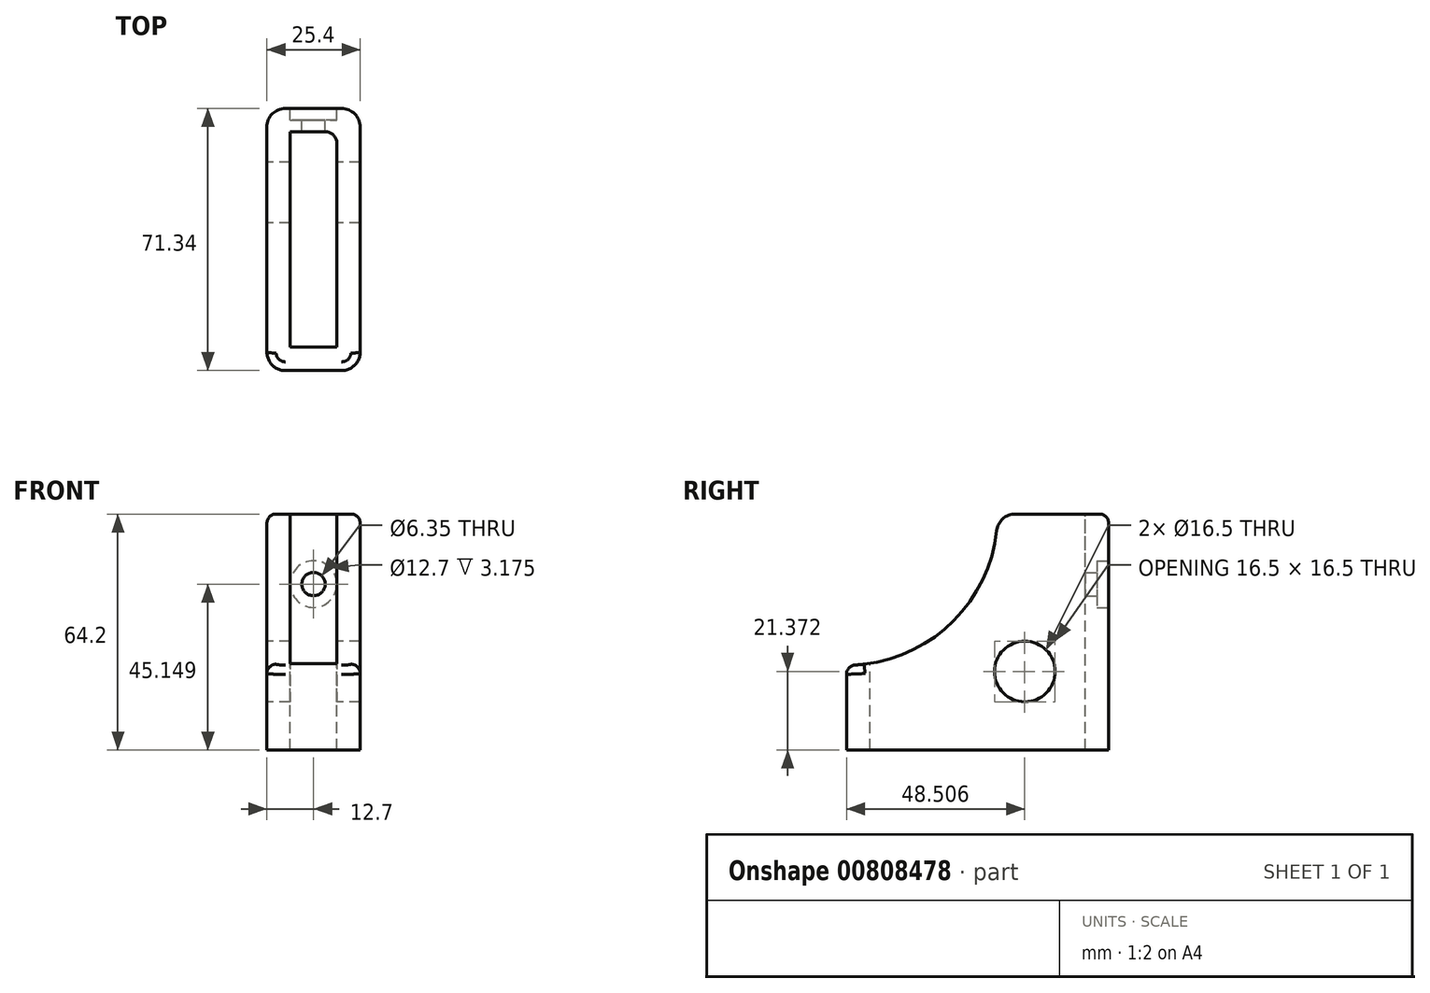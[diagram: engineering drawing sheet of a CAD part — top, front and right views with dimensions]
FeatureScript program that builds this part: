
annotation { "Feature Type Name" : "Feature", "Feature Type Description" : "" }
export const myFeature = defineFeature(function(context is Context, id is Id, definition is map)
    precondition{}
    {
        {
            var Q0;
            Q0=qCreatedBy(makeId("Right.planeOp"),FACE);
            var sketch = newSketch(context, id + "F0", { "sketchPlane" : qUnion([Q0])});
            skLineSegment(sketch, "E0", {"start": v(-41.12, 55.88) * mm, "end": v(-41.12, -8.32) * mm});
            skLineSegment(sketch, "E1", {"start": v(30.22, -8.32) * mm, "end": v(30.22, 55.88) * mm});
            skLineSegment(sketch, "E2", {"start": v(-41.12, 55.88) * mm, "end": v(30.22, 55.88) * mm});
            skLineSegment(sketch, "E3", {"start": v(-41.12, -8.32) * mm, "end": v(30.22, -8.32) * mm});
            skCircle(sketch, "E4", {"center": v(7.39, 13.05) * mm, "radius": 8.25 * mm});
            skSolve(sketch);
        }
        {
            var Q0;
            Q0 = qSketchRegion(id + "F0", true);
            extrude(context, id + "F1", {"entities" : qUnion([Q0]), "depth" : 25.4 * mm, "offsetDistance" : 25.4 * mm});
        }
        {
            var Q0;
            Q0=makeQuery(id+"F1.opExtrude","CAP_FACE",FACE,{"disambiguationData":[OSD([sQuery(id+"F0.wireOp",EDGE,"E0"),sQuery(id+"F0.wireOp",EDGE,"E1"),sQuery(id+"F0.wireOp",EDGE,"E2"),sQuery(id+"F0.wireOp",EDGE,"E3"),sQuery(id+"F0.wireOp",EDGE,"E4")])],"isStart":false});
            var sketch = newSketch(context, id + "F2", { "sketchPlane" : qUnion([Q0])});
            skCircle(sketch, "E5", {"center": v(-41.12, 55.88) * mm, "radius": 41.13 * mm});
            skSolve(sketch);
        }
        {
            var Q0;
            Q0 = qSketchRegion(id + "F2", true);
            extrude(context, id + "F3", {"entities" : qUnion([Q0]), "operationType" : NewBodyOperationType.REMOVE, "endBound" : BoundingType.THROUGH_ALL, "oppositeDirection" : true, "depth" : 25.4 * mm, "offsetDistance" : 25.4 * mm});
        }
        {
            var Q0;
            Q0=makeQuery(id+"F1.opExtrude","SWEPT_FACE",FACE,{"disambiguationData":[OSD([sQuery(id+"F0.wireOp",EDGE,"E2")])]});
            var sketch = newSketch(context, id + "F4", { "sketchPlane" : qUnion([Q0])});
            skLineSegment(sketch, "E6.bottom", {"start": v(6.35, 23.87) * mm, "end": v(19.05, 23.87) * mm});
            skLineSegment(sketch, "E6.top", {"start": v(6.35, -34.77) * mm, "end": v(19.05, -34.77) * mm});
            skLineSegment(sketch, "E6.left", {"start": v(6.35, 23.87) * mm, "end": v(6.35, -34.77) * mm});
            skLineSegment(sketch, "E6.right", {"start": v(19.05, 23.87) * mm, "end": v(19.05, -34.77) * mm});
            skSolve(sketch);
        }
        {
            var Q0;
            {var subQ0=sQuery(id+"F4.wireOp",EDGE,"E6.top");Q0=makeQuery(id+"F4.imprint","IMPRINT",FACE,{"disambiguationData":[TD([[makeQuery(id+"F4.imprint","IMPRINT",EDGE,{"derivedFrom":subQ0}),1.0]])]});}
            var Q1;
            {var subQ0=sQuery(id+"F4.wireOp",EDGE,"E6.bottom");Q1=makeQuery(id+"F4.imprint","IMPRINT",FACE,{"disambiguationData":[TD([[makeQuery(id+"F4.imprint","IMPRINT",EDGE,{"derivedFrom":subQ0}),-1.0]])]});}
            extrude(context, id + "F5", {"entities" : qUnion([Q0, Q1]), "operationType" : NewBodyOperationType.REMOVE, "endBound" : BoundingType.THROUGH_ALL, "oppositeDirection" : true, "depth" : 25.4 * mm, "offsetDistance" : 25.4 * mm});
        }
        {
            var Q0;
            {var subQ0=sQuery(id+"F0.wireOp",EDGE,"E2");var subQ1=makeQuery(id+"F1.opExtrude","SWEPT_FACE",FACE,{"disambiguationData":[OSD([subQ0])]});var subQ2=makeQuery(id+"F3.opExtrude","SWEPT_FACE",FACE,{"disambiguationData":[OSD([sQuery(id+"F2.wireOp",EDGE,"E5")])]});Q0=makeQuery(id+"F5.boolean.opBoolean","SPLIT",EDGE,{"disambiguationData":[TD([makeQuery(id+"F5.opExtrude","SWEPT_FACE",FACE,{"disambiguationData":[OSD([sQuery(id+"F4.wireOp",EDGE,"E6.left")])]})])],"derivedFrom":makeQuery(id+"F3.boolean.opBoolean","INTERSECT",EDGE,{"derivedFrom":[subQ1,subQ2]})});}
            var Q1;
            {var subQ0=sQuery(id+"F0.wireOp",EDGE,"E2");var subQ1=makeQuery(id+"F1.opExtrude","SWEPT_FACE",FACE,{"disambiguationData":[OSD([subQ0])]});var subQ2=makeQuery(id+"F3.opExtrude","SWEPT_FACE",FACE,{"disambiguationData":[OSD([sQuery(id+"F2.wireOp",EDGE,"E5")])]});Q1=makeQuery(id+"F5.boolean.opBoolean","SPLIT",EDGE,{"disambiguationData":[TD([makeQuery(id+"F5.opExtrude","SWEPT_FACE",FACE,{"disambiguationData":[OSD([sQuery(id+"F4.wireOp",EDGE,"E6.right")])]})])],"derivedFrom":makeQuery(id+"F3.boolean.opBoolean","INTERSECT",EDGE,{"derivedFrom":[subQ1,subQ2]})});}
            fillet(context, id + "F6", {"entities" : qUnion([Q0, Q1]), "radius" : 5.08 * mm, "tangentPropagation" : true, "allowEdgeOverflow" : false});
        }
        {
            var Q0;
            Q0=makeQuery(id+"F1.opExtrude","CAP_EDGE",EDGE,{"disambiguationData":[OSD([sQuery(id+"F0.wireOp",EDGE,"E1")])],"isStart":false});
            var Q1;
            Q1=makeQuery(id+"F1.opExtrude","CAP_EDGE",EDGE,{"disambiguationData":[OSD([sQuery(id+"F0.wireOp",EDGE,"E0")])],"isStart":false});
            var Q2;
            Q2=makeQuery(id+"F1.opExtrude","CAP_EDGE",EDGE,{"disambiguationData":[OSD([sQuery(id+"F0.wireOp",EDGE,"E0")])],"isStart":true});
            var Q3;
            Q3=makeQuery(id+"F1.opExtrude","CAP_EDGE",EDGE,{"disambiguationData":[OSD([sQuery(id+"F0.wireOp",EDGE,"E1")])],"isStart":true});
            fillet(context, id + "F7", {"entities" : qUnion([Q0, Q1, Q2, Q3]), "radius" : 5.08 * mm, "tangentPropagation" : true, "allowEdgeOverflow" : false});
        }
        {
            var Q0;
            Q0=makeQuery(id+"F3.boolean.opBoolean","COPY",EDGE,{"derivedFrom":makeQuery(id+"F3.opExtrude","CAP_EDGE",EDGE,{"disambiguationData":[OSD([sQuery(id+"F2.wireOp",EDGE,"E5")])],"isStart":true})});
            var Q1;
            {var subQ0=sQuery(id+"F0.wireOp",EDGE,"E2");var subQ1=makeQuery(id+"F1.opExtrude","CAP_FACE",FACE,{"disambiguationData":[OSD([sQuery(id+"F0.wireOp",EDGE,"E0"),sQuery(id+"F0.wireOp",EDGE,"E1"),subQ0,sQuery(id+"F0.wireOp",EDGE,"E3"),sQuery(id+"F0.wireOp",EDGE,"E4")])],"isStart":false});var subQ2=makeQuery(id+"F1.opExtrude","SWEPT_FACE",FACE,{"disambiguationData":[OSD([subQ0])]});var subQ3=makeQuery(id+"F3.opExtrude","SWEPT_FACE",FACE,{"disambiguationData":[OSD([sQuery(id+"F2.wireOp",EDGE,"E5")])]});Q1=makeQuery(id+"F6.opFillet","BLEND_EDGE",EDGE,{"blendedFrom":[makeQuery(id+"F5.boolean.opBoolean","SPLIT",EDGE,{"disambiguationData":[TD([makeQuery(id+"F5.opExtrude","SWEPT_FACE",FACE,{"disambiguationData":[OSD([sQuery(id+"F4.wireOp",EDGE,"E6.right")])]})])],"derivedFrom":makeQuery(id+"F3.boolean.opBoolean","INTERSECT",EDGE,{"derivedFrom":[subQ2,subQ3]})}),subQ1],"blendedInto":[subQ1]});}
            fillet(context, id + "F8", {"entities" : qUnion([Q0, Q1]), "radius" : 2.54 * mm, "tangentPropagation" : true, "allowEdgeOverflow" : false});
        }
        {
            var Q0;
            Q0=makeQuery(id+"F1.opExtrude","SWEPT_FACE",FACE,{"disambiguationData":[OSD([sQuery(id+"F0.wireOp",EDGE,"E1")])]});
            var sketch = newSketch(context, id + "F9", { "sketchPlane" : qUnion([Q0])});
            skPoint(sketch, "E7", {"position": v(-12.7, 36.83) * mm});
            skSolve(sketch);
        }
        {
            var Q0;
            Q0=sQuery(id+"F9.wireOp",VERTEX,"E7");
            var Q1;
            Q1=makeQuery(id+"F1.opExtrude","SWEPT_BODY",BODY,{"disambiguationData":[OSD([sQuery(id+"F0.wireOp",EDGE,"E0"),sQuery(id+"F0.wireOp",EDGE,"E1"),sQuery(id+"F0.wireOp",EDGE,"E2"),sQuery(id+"F0.wireOp",EDGE,"E3"),sQuery(id+"F0.wireOp",EDGE,"E4")])]});
            hole(context, id + "F10", {"style" : HoleStyle.C_BORE, "endStyle" : HoleEndStyle.THROUGH, "holeDiameter" : 6.35 * mm, "cBoreDiameter" : 12.7 * mm, "cBoreDepth" : 3.17 * mm, "majorDiameter" : 6.35 * mm, "isTappedThrough" : true, "tappedDepth" : 12.7 * mm, "tapClearance" : 3, "locations" : qUnion([Q0]), "scope" : qUnion([Q1])});
        }
        {
            var Q0;
            Q0=makeQuery(id+"F5.boolean.opBoolean","COPY",EDGE,{"derivedFrom":makeQuery(id+"F5.opExtrude","SWEPT_EDGE",EDGE,{"disambiguationData":[OSD([sQuery(id+"F4.wireOp",EDGE,"E6.bottom"),sQuery(id+"F4.wireOp",EDGE,"E6.right")])]})});
            fillet(context, id + "F11", {"entities" : qUnion([Q0]), "radius" : 3.17 * mm, "tangentPropagation" : true, "allowEdgeOverflow" : false});
        }
    });
